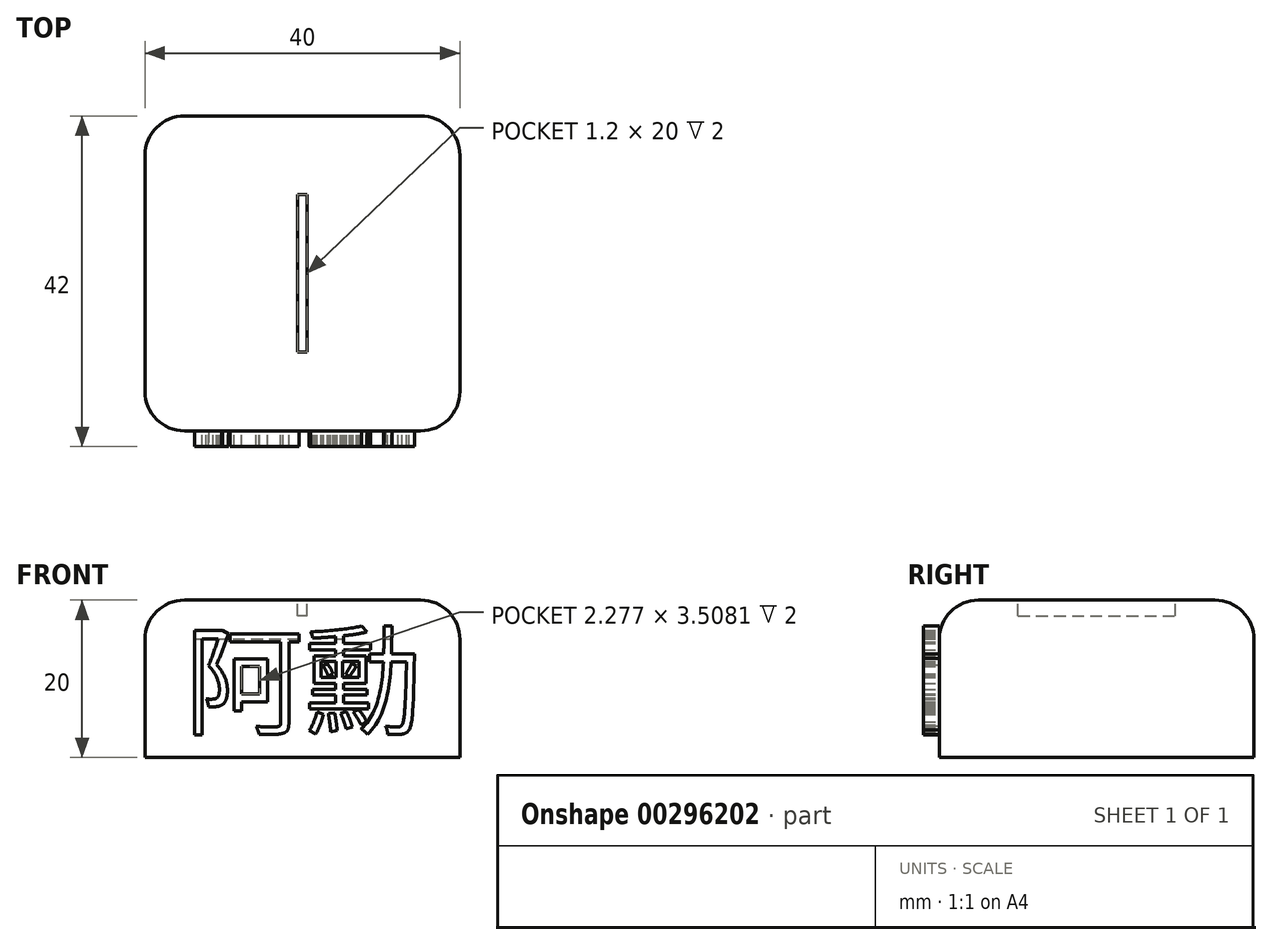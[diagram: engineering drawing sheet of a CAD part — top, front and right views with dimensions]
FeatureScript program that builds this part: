
annotation { "Feature Type Name" : "Feature", "Feature Type Description" : "" }
export const myFeature = defineFeature(function(context is Context, id is Id, definition is map)
    precondition{}
    {
        {
            var Q0;
            Q0=qCreatedBy(makeId("Top.planeOp"),FACE);
            var sketch = newSketch(context, id + "F0", { "sketchPlane" : qUnion([Q0])});
            skLineSegment(sketch, "E0.bottom", {"start": v(20, -20) * mm, "end": v(-20, -20) * mm});
            skLineSegment(sketch, "E0.top", {"start": v(20, 20) * mm, "end": v(-20, 20) * mm});
            skLineSegment(sketch, "E0.left", {"start": v(20, -20) * mm, "end": v(20, 20) * mm});
            skLineSegment(sketch, "E0.right", {"start": v(-20, -20) * mm, "end": v(-20, 20) * mm});
            skPoint(sketch, "E0.middle", {"position": v(0, 0) * mm});
            skLineSegment(sketch, "E1.bottom", {"start": v(0.6, -10) * mm, "end": v(-0.6, -10) * mm});
            skLineSegment(sketch, "E1.top", {"start": v(0.6, 10) * mm, "end": v(-0.6, 10) * mm});
            skLineSegment(sketch, "E1.left", {"start": v(0.6, -10) * mm, "end": v(0.6, 10) * mm});
            skLineSegment(sketch, "E1.right", {"start": v(-0.6, -10) * mm, "end": v(-0.6, 10) * mm});
            skSolve(sketch);
        }
        {
            var Q0;
            Q0=makeQuery(id+"F0.imprint","IMPRINT",FACE,{"disambiguationData":[TD([[makeQuery(id+"F0.imprint","IMPRINT",EDGE,{"derivedFrom":sQuery(id+"F0.wireOp",EDGE,"E0.bottom")}),-1.0]])]});
            var Q1;
            Q1=makeQuery(id+"F0.imprint","IMPRINT",FACE,{"disambiguationData":[TD([[makeQuery(id+"F0.imprint","IMPRINT",EDGE,{"derivedFrom":sQuery(id+"F0.wireOp",EDGE,"E1.bottom")}),-1.0]])]});
            extrude(context, id + "F1", {"entities" : qUnion([Q0, Q1]), "oppositeDirection" : true, "depth" : 20 * mm});
        }
        {
            var Q0;
            Q0=makeQuery(id+"F0.imprint","IMPRINT",FACE,{"disambiguationData":[TD([[makeQuery(id+"F0.imprint","IMPRINT",EDGE,{"derivedFrom":sQuery(id+"F0.wireOp",EDGE,"E1.bottom")}),-1.0]])]});
            extrude(context, id + "F2", {"entities" : qUnion([Q0]), "operationType" : NewBodyOperationType.REMOVE, "oppositeDirection" : true, "depth" : 2 * mm});
        }
        {
            var Q0;
            Q0=makeQuery(id+"F2.boolean.opBoolean","COPY",EDGE,{"derivedFrom":makeQuery(id+"F2.opExtrude","CAP_EDGE",EDGE,{"disambiguationData":[OSD([sQuery(id+"F0.wireOp",EDGE,"E1.left")])],"isStart":true})});
            var Q1;
            Q1=makeQuery(id+"F2.boolean.opBoolean","COPY",EDGE,{"derivedFrom":makeQuery(id+"F2.opExtrude","CAP_EDGE",EDGE,{"disambiguationData":[OSD([sQuery(id+"F0.wireOp",EDGE,"E1.right")])],"isStart":true})});
            var Q2;
            Q2=makeQuery(id+"F1.opExtrude","SWEPT_EDGE",EDGE,{"disambiguationData":[OSD([sQuery(id+"F0.wireOp",EDGE,"E0.bottom"),sQuery(id+"F0.wireOp",EDGE,"E0.left")])]});
            var Q3;
            Q3=makeQuery(id+"F1.opExtrude","SWEPT_EDGE",EDGE,{"disambiguationData":[OSD([sQuery(id+"F0.wireOp",EDGE,"E0.top"),sQuery(id+"F0.wireOp",EDGE,"E0.left")])]});
            var Q4;
            Q4=makeQuery(id+"F1.opExtrude","CAP_EDGE",EDGE,{"disambiguationData":[OSD([sQuery(id+"F0.wireOp",EDGE,"E0.left")])],"isStart":true});
            var Q5;
            Q5=makeQuery(id+"F1.opExtrude","SWEPT_EDGE",EDGE,{"disambiguationData":[OSD([sQuery(id+"F0.wireOp",EDGE,"E0.bottom"),sQuery(id+"F0.wireOp",EDGE,"E0.right")])]});
            var Q6;
            Q6=makeQuery(id+"F1.opExtrude","SWEPT_EDGE",EDGE,{"disambiguationData":[OSD([sQuery(id+"F0.wireOp",EDGE,"E0.top"),sQuery(id+"F0.wireOp",EDGE,"E0.right")])]});
            var Q7;
            Q7=makeQuery(id+"F1.opExtrude","CAP_EDGE",EDGE,{"disambiguationData":[OSD([sQuery(id+"F0.wireOp",EDGE,"E0.top")])],"isStart":true});
            var Q8;
            Q8=makeQuery(id+"F1.opExtrude","CAP_EDGE",EDGE,{"disambiguationData":[OSD([sQuery(id+"F0.wireOp",EDGE,"E0.right")])],"isStart":true});
            var Q9;
            Q9=makeQuery(id+"F1.opExtrude","CAP_EDGE",EDGE,{"disambiguationData":[OSD([sQuery(id+"F0.wireOp",EDGE,"E0.bottom")])],"isStart":true});
            fillet(context, id + "F3", {"entities" : qUnion([Q0, Q1, Q2, Q3, Q4, Q5, Q6, Q7, Q8, Q9]), "radius" : 5 * mm, "tangentPropagation" : true, "allowEdgeOverflow" : false});
        }
        {
            var Q0;
            Q0=makeQuery(id+"F1.opExtrude","SWEPT_FACE",FACE,{"disambiguationData":[OSD([sQuery(id+"F0.wireOp",EDGE,"E0.bottom")])]});
            var sketch = newSketch(context, id + "F4", { "sketchPlane" : qUnion([Q0])});
            skText(sketch, "E2", { "text": "阿勳", "fontName": "NotoSansCJKtc-Regular.otf"});
            const initialGuessF4  = {"E2": [-0.015, -0.01593, 1, 0, 0.01093]};
            skSetInitialGuess(sketch, initialGuessF4);
            skSolve(sketch);
        }
        {
            var Q0;
            {var subQ1=sQuery(id+"F4.wireOp",EDGE,"E2.sketch_text.stroke-30");Q0=makeQuery(id+"F4.imprint","IMPRINT",FACE,{"disambiguationData":[TD([[makeQuery(id+"F4.imprint","IMPRINT",EDGE,{"derivedFrom":subQ1}),1.0]])]});}
            var Q1;
            {var subQ0=sQuery(id+"F4.wireOp",EDGE,"E2.sketch_text.stroke-28");Q1=makeQuery(id+"F4.imprint","IMPRINT",FACE,{"disambiguationData":[TD([[makeQuery(id+"F4.imprint","IMPRINT",EDGE,{"derivedFrom":subQ0}),1.0]])]});}
            var Q2;
            Q2=makeQuery(id+"F4.imprint","IMPRINT",FACE,{"disambiguationData":[TD([[makeQuery(id+"F4.imprint","IMPRINT",EDGE,{"derivedFrom":sQuery(id+"F4.wireOp",EDGE,"E2.sketch_text.stroke-0")}),1.0]])]});
            var Q3;
            {var subQ0=sQuery(id+"F4.wireOp",EDGE,"E2.sketch_text.stroke-3");Q3=makeQuery(id+"F4.imprint","IMPRINT",FACE,{"disambiguationData":[TD([[makeQuery(id+"F4.imprint","IMPRINT",EDGE,{"derivedFrom":subQ0}),1.0]])]});}
            var Q4;
            {var subQ1=sQuery(id+"F4.wireOp",EDGE,"E2.sketch_text.stroke-7");Q4=makeQuery(id+"F4.imprint","IMPRINT",FACE,{"disambiguationData":[TD([[makeQuery(id+"F4.imprint","IMPRINT",EDGE,{"derivedFrom":subQ1}),1.0]])]});}
            var Q5;
            Q5=makeQuery(id+"F4.imprint","IMPRINT",FACE,{"disambiguationData":[TD([[makeQuery(id+"F4.imprint","IMPRINT",EDGE,{"derivedFrom":sQuery(id+"F4.wireOp",EDGE,"E2.sketch_text.stroke-18")}),1.0]])]});
            var Q6;
            {var subQ0=sQuery(id+"F4.wireOp",EDGE,"E2.sketch_text.stroke-82");Q6=makeQuery(id+"F4.imprint","IMPRINT",FACE,{"disambiguationData":[TD([[makeQuery(id+"F4.imprint","IMPRINT",EDGE,{"derivedFrom":subQ0}),1.0]])]});}
            var Q7;
            Q7=makeQuery(id+"F4.imprint","IMPRINT",FACE,{"disambiguationData":[TD([[makeQuery(id+"F4.imprint","IMPRINT",EDGE,{"derivedFrom":sQuery(id+"F4.wireOp",EDGE,"E2.sketch_text.stroke-48")}),1.0]])]});
            var Q8;
            Q8=makeQuery(id+"F4.imprint","IMPRINT",FACE,{"disambiguationData":[TD([[makeQuery(id+"F4.imprint","IMPRINT",EDGE,{"derivedFrom":sQuery(id+"F4.wireOp",EDGE,"E2.sketch_text.stroke-40")}),1.0]])]});
            var Q9;
            Q9=makeQuery(id+"F4.imprint","IMPRINT",FACE,{"disambiguationData":[TD([[makeQuery(id+"F4.imprint","IMPRINT",EDGE,{"derivedFrom":sQuery(id+"F4.wireOp",EDGE,"E2.sketch_text.stroke-96")}),1.0]])]});
            var Q10;
            Q10=makeQuery(id+"F4.imprint","IMPRINT",FACE,{"disambiguationData":[TD([[makeQuery(id+"F4.imprint","IMPRINT",EDGE,{"derivedFrom":sQuery(id+"F4.wireOp",EDGE,"E2.sketch_text.stroke-92")}),1.0]])]});
            var Q11;
            Q11=makeQuery(id+"F4.imprint","IMPRINT",FACE,{"disambiguationData":[TD([[makeQuery(id+"F4.imprint","IMPRINT",EDGE,{"derivedFrom":sQuery(id+"F4.wireOp",EDGE,"E2.sketch_text.stroke-100")}),1.0]])]});
            var Q12;
            Q12=makeQuery(id+"F4.imprint","IMPRINT",FACE,{"disambiguationData":[TD([[makeQuery(id+"F4.imprint","IMPRINT",EDGE,{"derivedFrom":sQuery(id+"F4.wireOp",EDGE,"E2.sketch_text.stroke-104")}),1.0]])]});
            var Q13;
            Q13=makeQuery(id+"F4.imprint","IMPRINT",FACE,{"disambiguationData":[TD([[makeQuery(id+"F4.imprint","IMPRINT",EDGE,{"derivedFrom":sQuery(id+"F4.wireOp",EDGE,"E2.sketch_text.stroke-44")}),1.0]])]});
            var Q14;
            {var subQ6=sQuery(id+"F4.wireOp",EDGE,"E2.sketch_text.stroke-108");Q14=makeQuery(id+"F4.imprint","IMPRINT",FACE,{"disambiguationData":[TD([[makeQuery(id+"F4.imprint","IMPRINT",EDGE,{"derivedFrom":subQ6}),1.0]])]});}
            var Q15;
            {var subQ0=sQuery(id+"F4.wireOp",EDGE,"E2.sketch_text.stroke-110");Q15=makeQuery(id+"F4.imprint","IMPRINT",FACE,{"disambiguationData":[TD([[makeQuery(id+"F4.imprint","IMPRINT",EDGE,{"derivedFrom":subQ0}),1.0]])]});}
            extrude(context, id + "F5", {"entities" : qUnion([Q0, Q1, Q2, Q3, Q4, Q5, Q6, Q7, Q8, Q9, Q10, Q11, Q12, Q13, Q14, Q15]), "operationType" : NewBodyOperationType.ADD, "depth" : 2 * mm});
        }
    });
